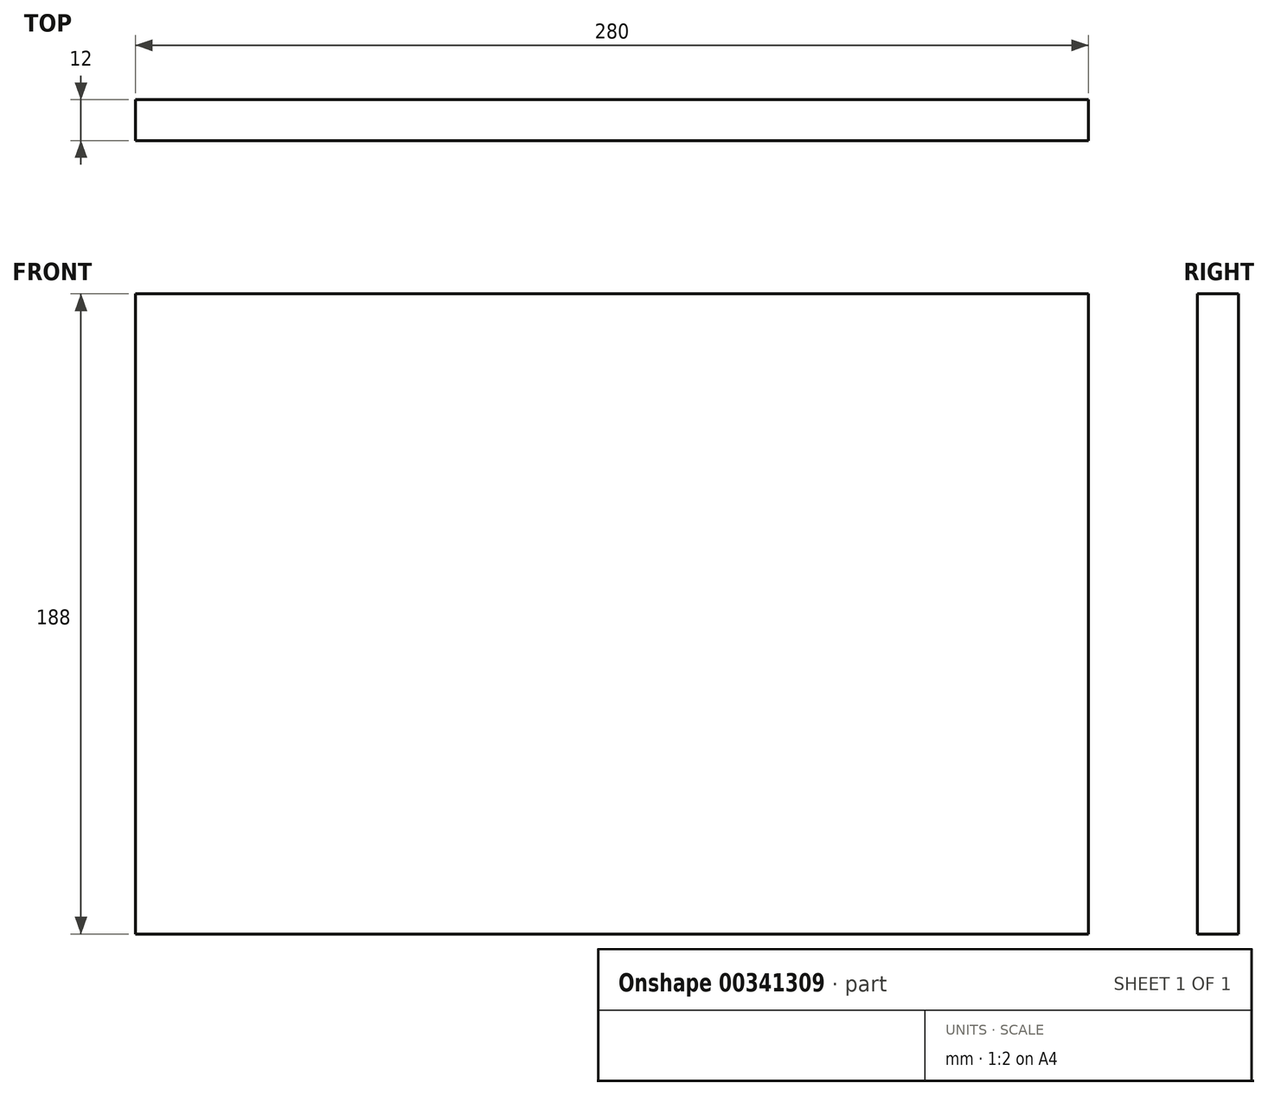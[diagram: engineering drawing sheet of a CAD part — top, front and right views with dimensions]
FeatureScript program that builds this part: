
annotation { "Feature Type Name" : "Feature", "Feature Type Description" : "" }
export const myFeature = defineFeature(function(context is Context, id is Id, definition is map)
    precondition{}
    {
        {
            var Q0;
            Q0=qCreatedBy(makeId("Front.planeOp"),FACE);
            var sketch = newSketch(context, id + "F0", { "sketchPlane" : qUnion([Q0])});
            skLineSegment(sketch, "E0.bottom", {"start": v(0, 0) * mm, "end": v(280, 0) * mm});
            skLineSegment(sketch, "E0.top", {"start": v(0, 188) * mm, "end": v(280, 188) * mm});
            skLineSegment(sketch, "E0.left", {"start": v(0, 0) * mm, "end": v(0, 188) * mm});
            skLineSegment(sketch, "E0.right", {"start": v(280, 0) * mm, "end": v(280, 188) * mm});
            skSolve(sketch);
        }
        {
            var Q0;
            Q0=makeQuery(id+"F0.imprint","IMPRINT",FACE,{"disambiguationData":[TD([[makeQuery(id+"F0.imprint","IMPRINT",EDGE,{"derivedFrom":sQuery(id+"F0.wireOp",EDGE,"E0.bottom")}),1.0]])]});
            extrude(context, id + "F1", {"entities" : qUnion([Q0]), "depth" : 12 * mm});
        }
    });
